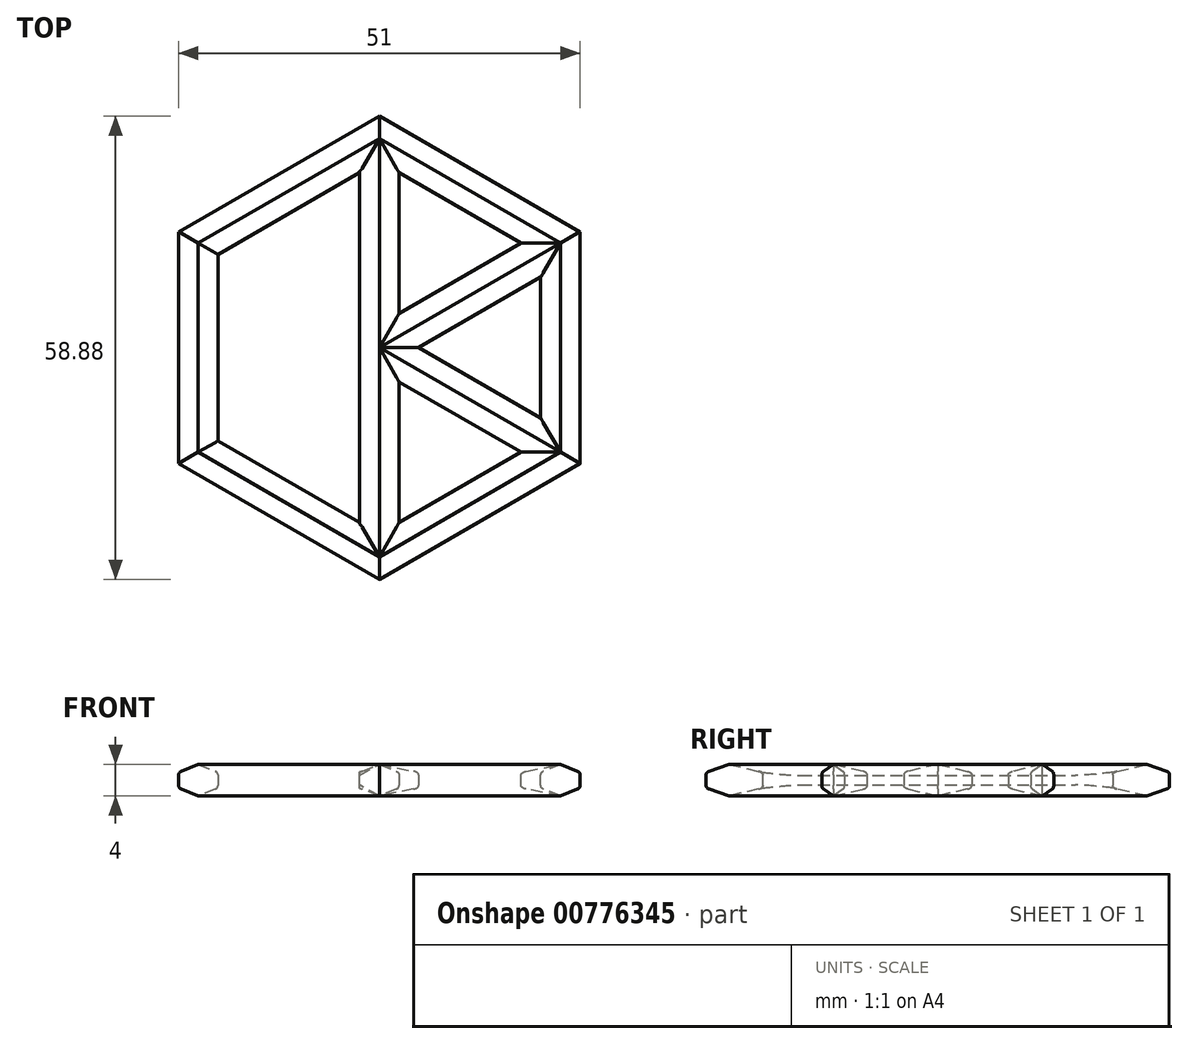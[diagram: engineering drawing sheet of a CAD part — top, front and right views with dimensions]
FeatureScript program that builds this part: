
annotation { "Feature Type Name" : "Feature", "Feature Type Description" : "" }
export const myFeature = defineFeature(function(context is Context, id is Id, definition is map)
    precondition{}
    {
        {
            var Q0;
            Q0=qCreatedBy(makeId("Top.planeOp"),FACE);
            var sketch = newSketch(context, id + "F0", { "sketchPlane" : qUnion([Q0])});
            skCircle(sketch, "E0.cCircle", {"center": v(0, 0) * mm, "radius": 29.44 * mm, "construction": true});
            skLineSegment(sketch, "E0.0", {"start": v(0, 29.44) * mm, "end": v(25.5, 14.72) * mm});
            skLineSegment(sketch, "E0.1", {"start": v(25.5, 14.72) * mm, "end": v(25.5, -14.72) * mm});
            skLineSegment(sketch, "E0.2", {"start": v(25.5, -14.72) * mm, "end": v(0, -29.44) * mm});
            skLineSegment(sketch, "E0.3", {"start": v(0, -29.44) * mm, "end": v(-25.5, -14.72) * mm});
            skLineSegment(sketch, "E0.4", {"start": v(-25.5, -14.72) * mm, "end": v(-25.5, 14.72) * mm});
            skLineSegment(sketch, "E0.5", {"start": v(-25.5, 14.72) * mm, "end": v(0, 29.44) * mm});
            skSolve(sketch);
        }
        {
            var Q0;
            Q0=qCreatedBy(makeId("Front.planeOp"),FACE);
            var sketch = newSketch(context, id + "F1", { "sketchPlane" : qUnion([Q0])});
            skLineSegment(sketch, "E1", {"start": v(-25.5, -1) * mm, "end": v(-25.5, 1) * mm});
            skLineSegment(sketch, "E2", {"start": v(-25.5, 1) * mm, "end": v(-23, 2) * mm});
            skLineSegment(sketch, "E3", {"start": v(-23, 2) * mm, "end": v(-20.5, 1) * mm});
            skLineSegment(sketch, "E4", {"start": v(-20.5, 1) * mm, "end": v(-20.5, -1) * mm});
            skLineSegment(sketch, "E5", {"start": v(-20.5, -1) * mm, "end": v(-23, -2) * mm});
            skLineSegment(sketch, "E6", {"start": v(-23, -2) * mm, "end": v(-25.5, -1) * mm});
            skLineSegment(sketch, "E7", {"start": v(-23, 2) * mm, "end": v(-23, -2) * mm});
            skPoint(sketch, "E8", {"position": v(-23, 0) * mm});
            skSolve(sketch);
        }
        {
            var Q0;
            Q0=qCreatedBy(makeId("Front.planeOp"),FACE);
            var sketch = newSketch(context, id + "F2", { "sketchPlane" : qUnion([Q0])});
            skLineSegment(sketch, "E9", {"start": v(-2.5, -1) * mm, "end": v(-2.5, 1) * mm});
            skLineSegment(sketch, "E10", {"start": v(-2.5, 1) * mm, "end": v(0, 2) * mm});
            skLineSegment(sketch, "E11", {"start": v(0, 2) * mm, "end": v(2.5, 1) * mm});
            skLineSegment(sketch, "E12", {"start": v(2.5, 1) * mm, "end": v(2.5, -1) * mm});
            skLineSegment(sketch, "E13", {"start": v(2.5, -1) * mm, "end": v(0, -2) * mm});
            skLineSegment(sketch, "E14", {"start": v(0, -2) * mm, "end": v(-2.5, -1) * mm});
            skLineSegment(sketch, "E15", {"start": v(0, 2) * mm, "end": v(0, -2) * mm});
            skPoint(sketch, "E16", {"position": v(0, 0) * mm});
            skSolve(sketch);
        }
        {
            var Q0;
            Q0=makeQuery(id+"F1.imprint","IMPRINT",FACE,{"disambiguationData":[TD([[makeQuery(id+"F1.imprint","IMPRINT",EDGE,{"derivedFrom":sQuery(id+"F1.wireOp",EDGE,"E1")}),-1.0]])]});
            var Q1;
            Q1=makeQuery(id+"F1.imprint","IMPRINT",FACE,{"disambiguationData":[TD([[makeQuery(id+"F1.imprint","IMPRINT",EDGE,{"derivedFrom":sQuery(id+"F1.wireOp",EDGE,"E3")}),-1.0]])]});
            var Q2;
            Q2=sQuery(id+"F0.wireOp",EDGE,"E0.4");
            var Q3;
            Q3=sQuery(id+"F0.wireOp",EDGE,"E0.3");
            var Q4;
            Q4=sQuery(id+"F0.wireOp",EDGE,"E0.2");
            var Q5;
            Q5=sQuery(id+"F0.wireOp",EDGE,"E0.1");
            var Q6;
            Q6=sQuery(id+"F0.wireOp",EDGE,"E0.0");
            var Q7;
            Q7=sQuery(id+"F0.wireOp",EDGE,"E0.5");
            sweep(context, id + "F3", {"profiles" : qUnion([Q0, Q1]), "path" : qUnion([Q2, Q3, Q4, Q5, Q6, Q7])});
        }
        {
            var Q0;
            Q0 = qSketchRegion(id + "F2", true);
            extrude(context, id + "F4", {"entities" : qUnion([Q0]), "endBound" : BoundingType.UP_TO_NEXT, "depth" : 28 * mm, "offsetDistance" : 25 * mm});
        }
        {
            var Q0;
            Q0=makeQuery(id+"F4.opExtrude","SWEPT_BODY",BODY,{"disambiguationData":[OSD([sQuery(id+"F2.wireOp",EDGE,"E9"),sQuery(id+"F2.wireOp",EDGE,"E10"),sQuery(id+"F2.wireOp",EDGE,"E11"),sQuery(id+"F2.wireOp",EDGE,"E12"),sQuery(id+"F2.wireOp",EDGE,"E13"),sQuery(id+"F2.wireOp",EDGE,"E14")])]});
            var Q1;
            Q1=sQuery(id+"F2.wireOp",EDGE,"E15");
            circularPattern(context, id + "F5", {"operationType" : NewBodyOperationType.ADD, "entities" : qUnion([Q0]), "axis" : qUnion([Q1]), "angle" : 180 * degree, "instanceCount" : 4, "oppositeDirection" : true, "equalSpace" : true});
        }
        {
            var Q0;
            Q0=qCreatedBy(makeId("Top.planeOp"),FACE);
            var sketch = newSketch(context, id + "F6", { "sketchPlane" : qUnion([Q0])});
            skLineSegment(sketch, "E17.bottom", {"start": v(-2.5, 22.23) * mm, "end": v(0, 26.56) * mm});
            skLineSegment(sketch, "E17.top", {"start": v(-2.5, -22.23) * mm, "end": v(0, -26.56) * mm});
            skLineSegment(sketch, "E17.left", {"start": v(-2.5, 22.23) * mm, "end": v(-2.5, -22.23) * mm});
            skLineSegment(sketch, "E17.right", {"start": v(0, 26.56) * mm, "end": v(0, -26.56) * mm});
            skSolve(sketch);
        }
        {
            var Q0;
            Q0=makeQuery(id+"F6.imprint","IMPRINT",FACE,{"disambiguationData":[TD([[makeQuery(id+"F6.imprint","IMPRINT",EDGE,{"derivedFrom":sQuery(id+"F6.wireOp",EDGE,"E17.bottom")}),-1.0]])]});
            extrude(context, id + "F7", {"entities" : qUnion([Q0]), "operationType" : NewBodyOperationType.REMOVE, "endBound" : BoundingType.SYMMETRIC, "depth" : 5 * mm, "offsetDistance" : 25 * mm});
        }
        {
            var Q0;
            Q0=qCreatedBy(makeId("Front.planeOp"),FACE);
            var sketch = newSketch(context, id + "F8", { "sketchPlane" : qUnion([Q0])});
            skLineSegment(sketch, "E18", {"start": v(-2.5, -0.63) * mm, "end": v(-2.5, 0.62) * mm});
            skLineSegment(sketch, "E19", {"start": v(-2.5, 0.62) * mm, "end": v(0, 2) * mm});
            skLineSegment(sketch, "E20", {"start": v(0, -2) * mm, "end": v(-2.5, -0.63) * mm});
            skLineSegment(sketch, "E21", {"start": v(0, 2) * mm, "end": v(0, -2) * mm});
            skPoint(sketch, "E22", {"position": v(0, 0) * mm});
            skSolve(sketch);
        }
        {
            var Q0;
            Q0=makeQuery(id+"F8.imprint","IMPRINT",FACE,{"disambiguationData":[TD([[makeQuery(id+"F8.imprint","IMPRINT",EDGE,{"derivedFrom":sQuery(id+"F8.wireOp",EDGE,"E18")}),-1.0]])]});
            extrude(context, id + "F9", {"entities" : qUnion([Q0]), "operationType" : NewBodyOperationType.ADD, "endBound" : BoundingType.SYMMETRIC, "depth" : 35 * mm, "offsetDistance" : 25 * mm});
        }
        {
            var Q1;
            Q1=makeQuery(id+"F7.boolean.opBoolean","COPY",FACE,{"derivedFrom":makeQuery(id+"F7.opExtrude","SWEPT_FACE",FACE,{"disambiguationData":[OSD([sQuery(id+"F6.wireOp",EDGE,"E17.bottom")])]})});
            var Q2;
            Q2=makeQuery(id+"F9.opExtrude","CAP_FACE",FACE,{"disambiguationData":[OSD([sQuery(id+"F8.wireOp",EDGE,"E18"),sQuery(id+"F8.wireOp",EDGE,"E19"),sQuery(id+"F8.wireOp",EDGE,"E20"),sQuery(id+"F8.wireOp",EDGE,"E21")])],"isStart":true});
            loft(context, id + "F10", {"operationType" : NewBodyOperationType.ADD, "endCondition" : LoftEndDerivativeType.NORMAL_TO_PROFILE, "endMagnitude" : 1, "sheetProfilesArray" : [{ "sheetProfileEntities" : qUnion([Q1]) }, { "sheetProfileEntities" : qUnion([Q2]) }]});
        }
        {
            var Q1;
            Q1=makeQuery(id+"F7.boolean.opBoolean","COPY",FACE,{"derivedFrom":makeQuery(id+"F7.opExtrude","SWEPT_FACE",FACE,{"disambiguationData":[OSD([sQuery(id+"F6.wireOp",EDGE,"E17.top")])]})});
            var Q2;
            Q2=makeQuery(id+"F9.opExtrude","CAP_FACE",FACE,{"disambiguationData":[OSD([sQuery(id+"F8.wireOp",EDGE,"E18"),sQuery(id+"F8.wireOp",EDGE,"E19"),sQuery(id+"F8.wireOp",EDGE,"E20"),sQuery(id+"F8.wireOp",EDGE,"E21")])],"isStart":false});
            loft(context, id + "F11", {"operationType" : NewBodyOperationType.ADD, "endCondition" : LoftEndDerivativeType.NORMAL_TO_PROFILE, "endMagnitude" : 1, "sheetProfilesArray" : [{ "sheetProfileEntities" : qUnion([Q1]) }, { "sheetProfileEntities" : qUnion([Q2]) }]});
        }
        {
            var Q0;
            Q0=makeQuery(id+"F5.opPattern","COPY",EDGE,{"derivedFrom":makeQuery(id+"F4.opExtrude","SWEPT_EDGE",EDGE,{"disambiguationData":[OSD([sQuery(id+"F2.wireOp",EDGE,"E12"),sQuery(id+"F2.wireOp",EDGE,"E13")])]}),"instanceName":"1"});
            var Q1;
            Q1=makeQuery(id+"F5.opPattern","COPY",EDGE,{"derivedFrom":makeQuery(id+"F4.opExtrude","SWEPT_EDGE",EDGE,{"disambiguationData":[OSD([sQuery(id+"F2.wireOp",EDGE,"E9"),sQuery(id+"F2.wireOp",EDGE,"E14")])]}),"instanceName":"2"});
            var Q2;
            Q2=makeQuery(id+"F3.opSweep","SWEPT_EDGE",EDGE,{"disambiguationData":[OSD([sQuery(id+"F0.wireOp",EDGE,"E0.1"),sQuery(id+"F1.wireOp",EDGE,"E4"),sQuery(id+"F1.wireOp",EDGE,"E5")])]});
            var Q3;
            Q3=makeQuery(id+"F4.opExtrude","SWEPT_EDGE",EDGE,{"disambiguationData":[OSD([sQuery(id+"F2.wireOp",EDGE,"E12"),sQuery(id+"F2.wireOp",EDGE,"E13")])]});
            var Q4;
            Q4=makeQuery(id+"F3.opSweep","SWEPT_EDGE",EDGE,{"disambiguationData":[OSD([sQuery(id+"F0.wireOp",EDGE,"E0.2"),sQuery(id+"F1.wireOp",EDGE,"E4"),sQuery(id+"F1.wireOp",EDGE,"E5")])]});
            var Q5;
            Q5=makeQuery(id+"F5.opPattern","COPY",EDGE,{"derivedFrom":makeQuery(id+"F4.opExtrude","SWEPT_EDGE",EDGE,{"disambiguationData":[OSD([sQuery(id+"F2.wireOp",EDGE,"E12"),sQuery(id+"F2.wireOp",EDGE,"E13")])]}),"instanceName":"2"});
            var Q6;
            Q6=makeQuery(id+"F3.opSweep","SWEPT_EDGE",EDGE,{"disambiguationData":[OSD([sQuery(id+"F0.wireOp",EDGE,"E0.0"),sQuery(id+"F1.wireOp",EDGE,"E4"),sQuery(id+"F1.wireOp",EDGE,"E5")])]});
            var Q7;
            Q7=makeQuery(id+"F5.opPattern","COPY",EDGE,{"derivedFrom":makeQuery(id+"F4.opExtrude","SWEPT_EDGE",EDGE,{"disambiguationData":[OSD([sQuery(id+"F2.wireOp",EDGE,"E9"),sQuery(id+"F2.wireOp",EDGE,"E14")])]}),"instanceName":"3"});
            var Q8;
            Q8=makeQuery(id+"F5.opPattern","COPY",EDGE,{"derivedFrom":makeQuery(id+"F4.opExtrude","SWEPT_EDGE",EDGE,{"disambiguationData":[OSD([sQuery(id+"F2.wireOp",EDGE,"E9"),sQuery(id+"F2.wireOp",EDGE,"E10")])]}),"instanceName":"3"});
            var Q9;
            Q9=makeQuery(id+"F5.opPattern","COPY",EDGE,{"derivedFrom":makeQuery(id+"F4.opExtrude","SWEPT_EDGE",EDGE,{"disambiguationData":[OSD([sQuery(id+"F2.wireOp",EDGE,"E11"),sQuery(id+"F2.wireOp",EDGE,"E12")])]}),"instanceName":"2"});
            var Q10;
            Q10=makeQuery(id+"F5.opPattern","COPY",EDGE,{"derivedFrom":makeQuery(id+"F4.opExtrude","SWEPT_EDGE",EDGE,{"disambiguationData":[OSD([sQuery(id+"F2.wireOp",EDGE,"E11"),sQuery(id+"F2.wireOp",EDGE,"E12")])]}),"instanceName":"1"});
            var Q11;
            Q11=makeQuery(id+"F5.opPattern","COPY",EDGE,{"derivedFrom":makeQuery(id+"F4.opExtrude","SWEPT_EDGE",EDGE,{"disambiguationData":[OSD([sQuery(id+"F2.wireOp",EDGE,"E9"),sQuery(id+"F2.wireOp",EDGE,"E10")])]}),"instanceName":"2"});
            var Q12;
            Q12=makeQuery(id+"F3.opSweep","SWEPT_EDGE",EDGE,{"disambiguationData":[OSD([sQuery(id+"F0.wireOp",EDGE,"E0.1"),sQuery(id+"F1.wireOp",EDGE,"E3"),sQuery(id+"F1.wireOp",EDGE,"E4")])]});
            var Q13;
            Q13=makeQuery(id+"F5.opPattern","COPY",EDGE,{"derivedFrom":makeQuery(id+"F4.opExtrude","SWEPT_EDGE",EDGE,{"disambiguationData":[OSD([sQuery(id+"F2.wireOp",EDGE,"E9"),sQuery(id+"F2.wireOp",EDGE,"E10")])]}),"instanceName":"1"});
            var Q14;
            Q14=makeQuery(id+"F3.opSweep","SWEPT_EDGE",EDGE,{"disambiguationData":[OSD([sQuery(id+"F0.wireOp",EDGE,"E0.2"),sQuery(id+"F1.wireOp",EDGE,"E3"),sQuery(id+"F1.wireOp",EDGE,"E4")])]});
            var Q15;
            Q15=makeQuery(id+"F4.opExtrude","SWEPT_EDGE",EDGE,{"disambiguationData":[OSD([sQuery(id+"F2.wireOp",EDGE,"E11"),sQuery(id+"F2.wireOp",EDGE,"E12")])]});
            var Q16;
            Q16=makeQuery(id+"F3.opSweep","SWEPT_EDGE",EDGE,{"disambiguationData":[OSD([sQuery(id+"F0.wireOp",EDGE,"E0.0"),sQuery(id+"F1.wireOp",EDGE,"E3"),sQuery(id+"F1.wireOp",EDGE,"E4")])]});
            var Q17;
            Q17=makeQuery(id+"F5.opPattern","COPY",EDGE,{"derivedFrom":makeQuery(id+"F4.opExtrude","SWEPT_EDGE",EDGE,{"disambiguationData":[OSD([sQuery(id+"F2.wireOp",EDGE,"E9"),sQuery(id+"F2.wireOp",EDGE,"E14")])]}),"instanceName":"1"});
            var Q18;
            Q18=makeQuery(id+"F3.opSweep","SWEPT_EDGE",EDGE,{"disambiguationData":[OSD([sQuery(id+"F0.wireOp",EDGE,"E0.3"),sQuery(id+"F1.wireOp",EDGE,"E3"),sQuery(id+"F1.wireOp",EDGE,"E4")])]});
            var Q19;
            Q19=makeQuery(id+"F3.opSweep","SWEPT_EDGE",EDGE,{"disambiguationData":[OSD([sQuery(id+"F0.wireOp",EDGE,"E0.3"),sQuery(id+"F1.wireOp",EDGE,"E4"),sQuery(id+"F1.wireOp",EDGE,"E5")])]});
            var Q20;
            Q20=makeQuery(id+"F3.opSweep","SWEPT_EDGE",EDGE,{"disambiguationData":[OSD([sQuery(id+"F0.wireOp",EDGE,"E0.4"),sQuery(id+"F1.wireOp",EDGE,"E4"),sQuery(id+"F1.wireOp",EDGE,"E5")])]});
            var Q21;
            Q21=makeQuery(id+"F3.opSweep","SWEPT_EDGE",EDGE,{"disambiguationData":[OSD([sQuery(id+"F0.wireOp",EDGE,"E0.4"),sQuery(id+"F1.wireOp",EDGE,"E3"),sQuery(id+"F1.wireOp",EDGE,"E4")])]});
            var Q22;
            Q22=makeQuery(id+"F3.opSweep","SWEPT_EDGE",EDGE,{"disambiguationData":[OSD([sQuery(id+"F0.wireOp",EDGE,"E0.5"),sQuery(id+"F1.wireOp",EDGE,"E4"),sQuery(id+"F1.wireOp",EDGE,"E5")])]});
            var Q23;
            Q23=makeQuery(id+"F3.opSweep","SWEPT_EDGE",EDGE,{"disambiguationData":[OSD([sQuery(id+"F0.wireOp",EDGE,"E0.5"),sQuery(id+"F1.wireOp",EDGE,"E3"),sQuery(id+"F1.wireOp",EDGE,"E4")])]});
            fillet(context, id + "F12", {"entities" : qUnion([Q0, Q1, Q2, Q3, Q4, Q5, Q6, Q7, Q8, Q9, Q10, Q11, Q12, Q13, Q14, Q15, Q16, Q17, Q18, Q19, Q20, Q21, Q22, Q23]), "radius" : .5 * mm, "tangentPropagation" : true, "allowEdgeOverflow" : false});
        }
        {
            var Q0;
            Q0=makeQuery(id+"F3.opSweep","SWEPT_EDGE",EDGE,{"disambiguationData":[OSD([sQuery(id+"F0.wireOp",EDGE,"E0.2"),sQuery(id+"F1.wireOp",EDGE,"E1"),sQuery(id+"F1.wireOp",EDGE,"E6")])]});
            var Q1;
            Q1=makeQuery(id+"F3.opSweep","SWEPT_EDGE",EDGE,{"disambiguationData":[OSD([sQuery(id+"F0.wireOp",EDGE,"E0.1"),sQuery(id+"F1.wireOp",EDGE,"E1"),sQuery(id+"F1.wireOp",EDGE,"E6")])]});
            var Q2;
            Q2=makeQuery(id+"F3.opSweep","SWEPT_EDGE",EDGE,{"disambiguationData":[OSD([sQuery(id+"F0.wireOp",EDGE,"E0.0"),sQuery(id+"F1.wireOp",EDGE,"E1"),sQuery(id+"F1.wireOp",EDGE,"E6")])]});
            var Q3;
            Q3=makeQuery(id+"F3.opSweep","SWEPT_EDGE",EDGE,{"disambiguationData":[OSD([sQuery(id+"F0.wireOp",EDGE,"E0.5"),sQuery(id+"F1.wireOp",EDGE,"E1"),sQuery(id+"F1.wireOp",EDGE,"E6")])]});
            var Q4;
            Q4=makeQuery(id+"F3.opSweep","SWEPT_EDGE",EDGE,{"disambiguationData":[OSD([sQuery(id+"F0.wireOp",EDGE,"E0.4"),sQuery(id+"F1.wireOp",EDGE,"E1"),sQuery(id+"F1.wireOp",EDGE,"E6")])]});
            var Q5;
            Q5=makeQuery(id+"F3.opSweep","SWEPT_EDGE",EDGE,{"disambiguationData":[OSD([sQuery(id+"F0.wireOp",EDGE,"E0.3"),sQuery(id+"F1.wireOp",EDGE,"E1"),sQuery(id+"F1.wireOp",EDGE,"E6")])]});
            var Q6;
            Q6=makeQuery(id+"F3.opSweep","SWEPT_EDGE",EDGE,{"disambiguationData":[OSD([sQuery(id+"F0.wireOp",EDGE,"E0.3"),sQuery(id+"F1.wireOp",EDGE,"E1"),sQuery(id+"F1.wireOp",EDGE,"E2")])]});
            var Q7;
            Q7=makeQuery(id+"F3.opSweep","SWEPT_EDGE",EDGE,{"disambiguationData":[OSD([sQuery(id+"F0.wireOp",EDGE,"E0.4"),sQuery(id+"F1.wireOp",EDGE,"E1"),sQuery(id+"F1.wireOp",EDGE,"E2")])]});
            var Q8;
            Q8=makeQuery(id+"F3.opSweep","SWEPT_EDGE",EDGE,{"disambiguationData":[OSD([sQuery(id+"F0.wireOp",EDGE,"E0.5"),sQuery(id+"F1.wireOp",EDGE,"E1"),sQuery(id+"F1.wireOp",EDGE,"E2")])]});
            var Q9;
            Q9=makeQuery(id+"F3.opSweep","SWEPT_EDGE",EDGE,{"disambiguationData":[OSD([sQuery(id+"F0.wireOp",EDGE,"E0.1"),sQuery(id+"F1.wireOp",EDGE,"E1"),sQuery(id+"F1.wireOp",EDGE,"E2")])]});
            var Q10;
            Q10=makeQuery(id+"F3.opSweep","SWEPT_EDGE",EDGE,{"disambiguationData":[OSD([sQuery(id+"F0.wireOp",EDGE,"E0.0"),sQuery(id+"F1.wireOp",EDGE,"E1"),sQuery(id+"F1.wireOp",EDGE,"E2")])]});
            var Q11;
            Q11=makeQuery(id+"F3.opSweep","SWEPT_EDGE",EDGE,{"disambiguationData":[OSD([sQuery(id+"F0.wireOp",EDGE,"E0.2"),sQuery(id+"F1.wireOp",EDGE,"E1"),sQuery(id+"F1.wireOp",EDGE,"E2")])]});
            fillet(context, id + "F13", {"entities" : qUnion([Q0, Q1, Q2, Q3, Q4, Q5, Q6, Q7, Q8, Q9, Q10, Q11]), "radius" : .5 * mm, "tangentPropagation" : true, "allowEdgeOverflow" : false});
        }
    });
